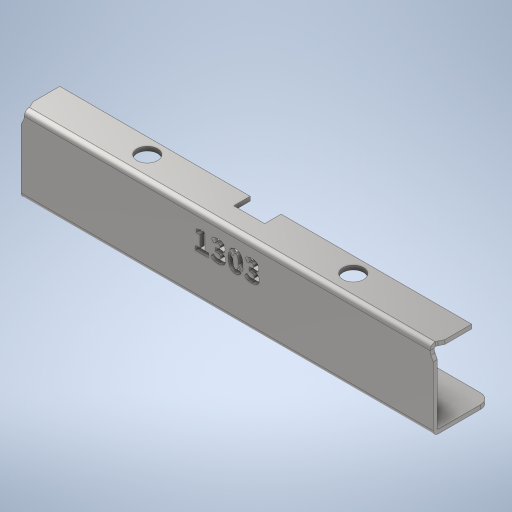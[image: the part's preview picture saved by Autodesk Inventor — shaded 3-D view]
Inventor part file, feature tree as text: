
AUTODESK INVENTOR PART (.ipt)
format: ipt  version: 2023 (Build 270158000, 158)  size: 693,760 bytes
history: native  units: mm
features: other x4, extrude x3, fillet x1, sketch x1, projected_geometry x1
ambient origin geometry x8: Origin, YZ Plane, XZ Plane, XY Plane, X Axis, Y Axis, Z Axis, Center Point
bodies: Body1 (feature_tree)
feature tree (10):
  other  "實體1"
  extrude  "擠出1"  Depth=200.0mm
  extrude  "擠出3"  Depth=26.3mm
  extrude  "擠出4"  Depth=33.0mm
  other  "折彎零件1"
  other  "折彎零件2"
  fillet  "圓角1"  Radius=17.0mm
  sketch  "草圖4"
  projected_geometry  "投影迴路1"
  other  "定義1"
